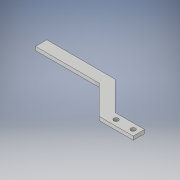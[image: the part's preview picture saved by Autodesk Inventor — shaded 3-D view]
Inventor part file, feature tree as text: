
AUTODESK INVENTOR PART (.ipt)
format: ipt  version: 2019 (Build 230136000, 136)  size: 115,200 bytes
history: native  units: mm
features: extrude x1, sketch x1
ambient origin geometry x8: Origin, YZ Plane, XZ Plane, XY Plane, X Axis, Y Axis, Z Axis, Center Point
bodies: Body1 (feature_tree)
feature tree (2):
  extrude  "Extrusion4"  Depth=60.0mm
  sketch  "Sketch1"  dims[d0=10.0mm d1=60.0mm d2=135.0deg d3=40.0mm d4=10.0mm d14=45.0deg d15=10.0mm d16=30.0mm d17=4.0mm d18=10.0mm d19=5.0mm d22=4.0mm d23=5.0mm d24=5.0mm d25=3.18mm d26=0.0mm]
